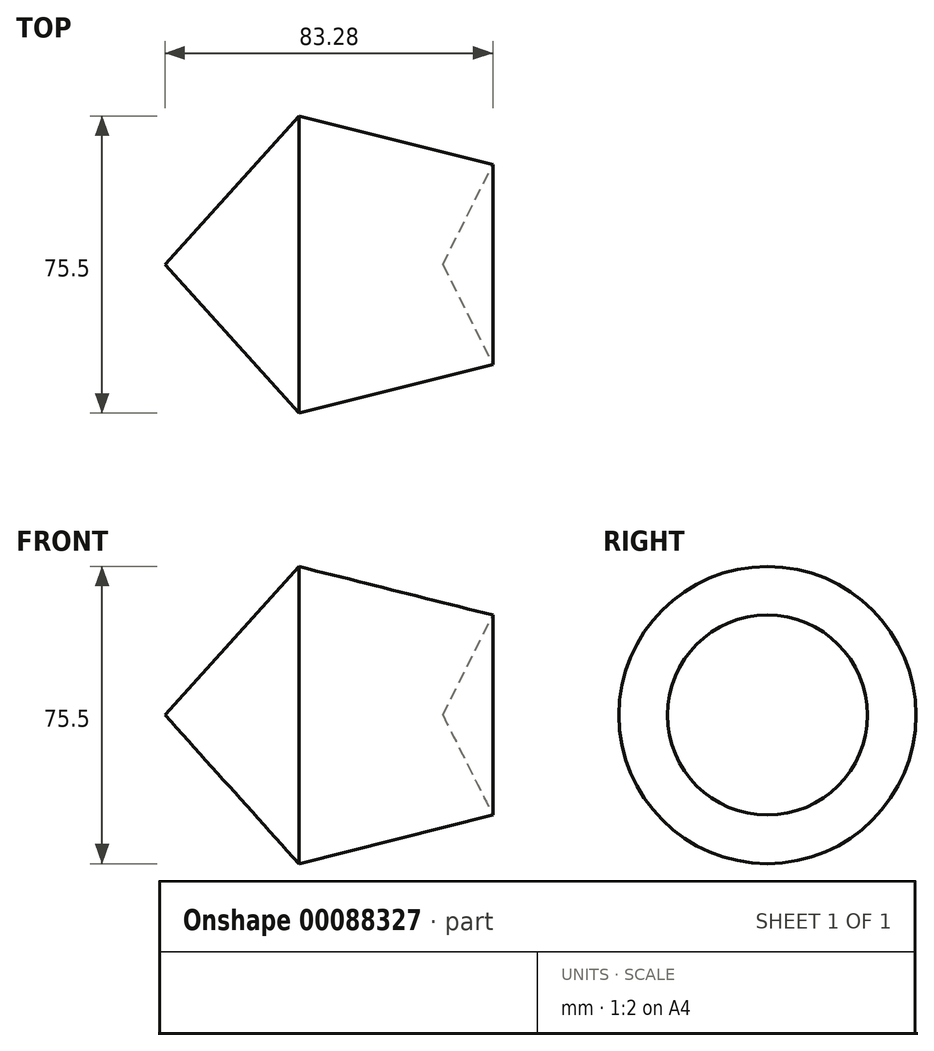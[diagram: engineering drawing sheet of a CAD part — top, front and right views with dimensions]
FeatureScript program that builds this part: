
annotation { "Feature Type Name" : "Feature", "Feature Type Description" : "" }
export const myFeature = defineFeature(function(context is Context, id is Id, definition is map)
    precondition{}
    {
        {
            var Q0;
            Q0=qCreatedBy(makeId("Front.planeOp"),FACE);
            var sketch = newSketch(context, id + "F0", { "sketchPlane" : qUnion([Q0])});
            skPoint(sketch, "E0", {"position": v(-12.7, 0) * mm});
            skPoint(sketch, "E1", {"position": v(12.7, 0) * mm});
            skPoint(sketch, "E2", {"position": v(0, 25.4) * mm});
            skPoint(sketch, "E3", {"position": v(0, -25.4) * mm});
            skLineSegment(sketch, "E4", {"start": v(0, 25.4) * mm, "end": v(-12.7, 0) * mm});
            skLineSegment(sketch, "E5", {"start": v(-12.7, 0) * mm, "end": v(0, -25.4) * mm});
            skLineSegment(sketch, "E6", {"start": v(0, -25.4) * mm, "end": v(12.7, 0) * mm});
            skLineSegment(sketch, "E7", {"start": v(12.7, 0) * mm, "end": v(0, 25.4) * mm});
            skLineSegment(sketch, "E8", {"start": v(0, 25.4) * mm, "end": v(0, 30.48) * mm});
            skLineSegment(sketch, "E9", {"start": v(0, 25.4) * mm, "end": v(-49.28, 37.75) * mm});
            skLineSegment(sketch, "E10", {"start": v(-49.28, 37.75) * mm, "end": v(-83.28, 0) * mm});
            skLineSegment(sketch, "E11", {"start": v(-83.28, 0) * mm, "end": v(-12.7, 0) * mm});
            skLineSegment(sketch, "E12", {"start": v(-12.7, 0) * mm, "end": v(0, 0) * mm});
            skLineSegment(sketch, "E13", {"start": v(0, 0) * mm, "end": v(0, 25.4) * mm});
            skSolve(sketch);
        }
        {
            var Q0;
            Q0=makeQuery(id+"F0.imprint","IMPRINT",FACE,{"disambiguationData":[TD([[makeQuery(id+"F0.imprint","IMPRINT",EDGE,{"derivedFrom":sQuery(id+"F0.wireOp",EDGE,"E4")}),-1.0]])]});
            var Q1;
            Q1=sQuery(id+"F0.wireOp",EDGE,"E11");
            revolve(context, id + "F1", {"entities" : qUnion([Q0]), "axis" : qUnion([Q1]), "revolveType" : RevolveType.FULL});
        }
    });
